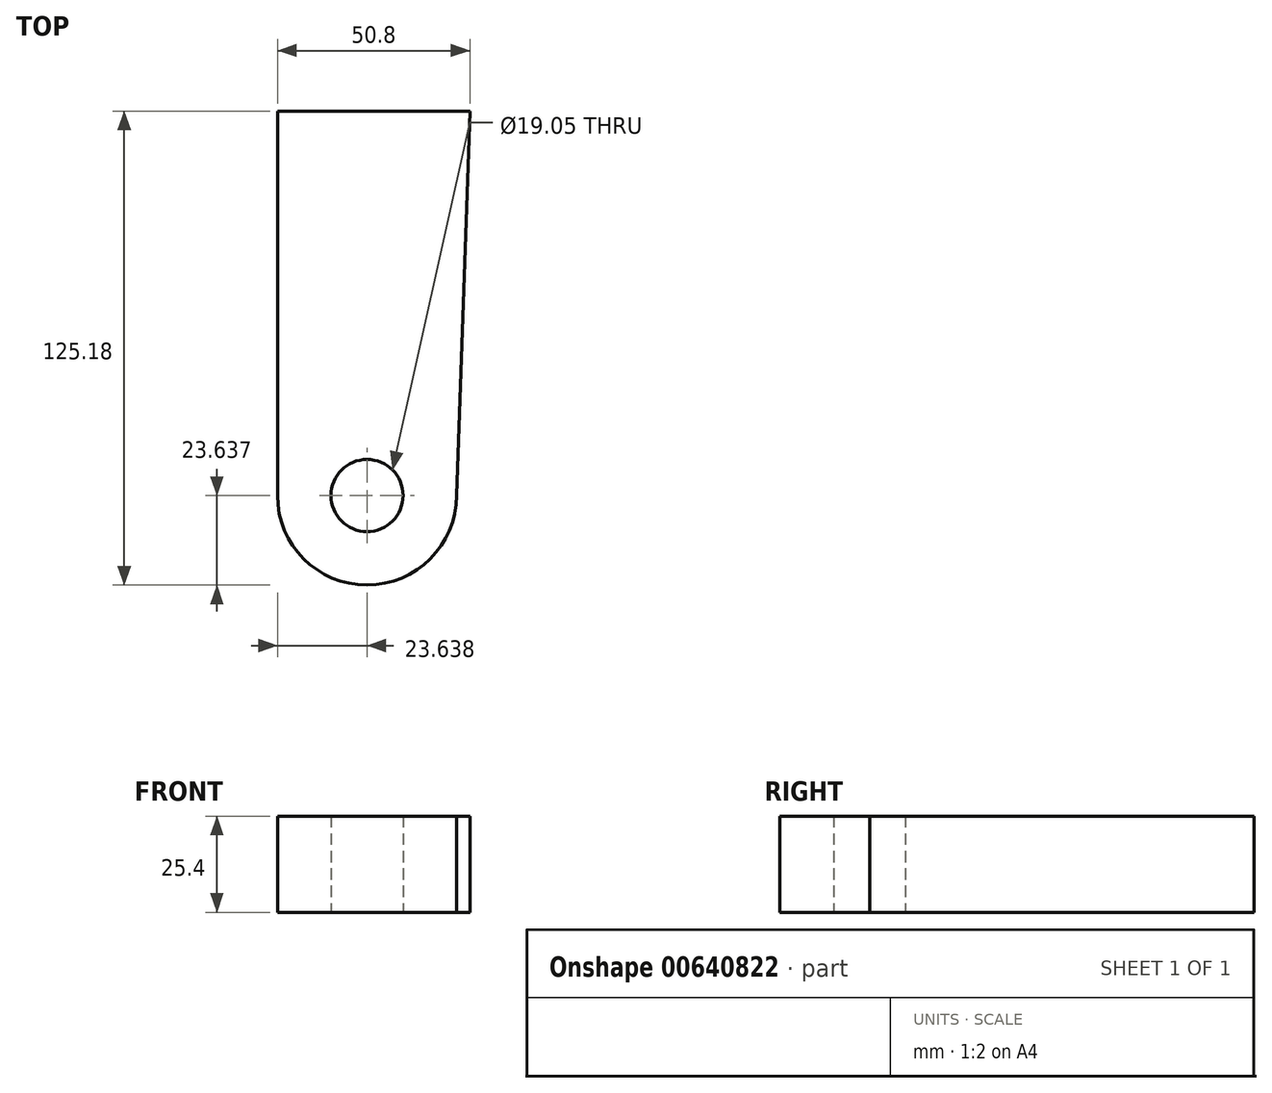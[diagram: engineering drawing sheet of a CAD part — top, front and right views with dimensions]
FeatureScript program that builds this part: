
annotation { "Feature Type Name" : "Feature", "Feature Type Description" : "" }
export const myFeature = defineFeature(function(context is Context, id is Id, definition is map)
    precondition{}
    {
        {
            var Q0;
            Q0=qCreatedBy(makeId("Top.planeOp"),FACE);
            var sketch = newSketch(context, id + "F0", { "sketchPlane" : qUnion([Q0])});
            skLineSegment(sketch, "E0", {"start": v(-24.4, -27.17) * mm, "end": v(22.9, -27.17) * mm});
            skLineSegment(sketch, "E1", {"start": v(22.9, -27.17) * mm, "end": v(26.4, 74.37) * mm});
            skLineSegment(sketch, "E2", {"start": v(26.4, 74.37) * mm, "end": v(-24.4, 74.37) * mm});
            skLineSegment(sketch, "E3", {"start": v(-24.4, 74.37) * mm, "end": v(-24.4, -27.17) * mm});
            skArc(sketch, "E4", {"start": v(-24.4, -27.17) * mm, "mid": v(-0.75, -50.81) * mm, "end": v(22.9, -27.17) * mm});
            skCircle(sketch, "E5", {"center": v(-0.75, -27.17) * mm, "radius": 9.53 * mm});
            skSolve(sketch);
        }
        {
            var Q0;
            {var subQ0=sQuery(id+"F0.wireOp",EDGE,"E1");Q0=makeQuery(id+"F0.imprint","IMPRINT",FACE,{"disambiguationData":[TD([[makeQuery(id+"F0.imprint","IMPRINT",EDGE,{"derivedFrom":subQ0}),1.0]])]});}
            var Q1;
            {var subQ0=sQuery(id+"F0.wireOp",EDGE,"E4");Q1=makeQuery(id+"F0.imprint","IMPRINT",FACE,{"disambiguationData":[TD([[makeQuery(id+"F0.imprint","IMPRINT",EDGE,{"derivedFrom":subQ0}),1.0]])]});}
            extrude(context, id + "F1", {"entities" : qUnion([Q0, Q1]), "depth" : 25.4 * mm, "offsetDistance" : 25.4 * mm});
        }
    });
